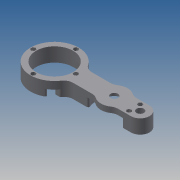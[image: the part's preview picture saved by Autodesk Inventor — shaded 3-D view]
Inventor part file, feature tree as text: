
AUTODESK INVENTOR PART (.ipt)
format: ipt  version: 2013 (Build 170138000, 138)  size: 330,752 bytes
history: native  units: mm
features: extrude x18, sketch x18, pattern_circular x2, fillet x2, projected_geometry x2, mirror x1
ambient origin geometry x8: Origin, YZ Plane, XZ Plane, XY Plane, X Axis, Y Axis, Z Axis, Center Point
bodies: Solid1 (feature_tree)
feature tree (43):
  extrude  "Extrusion1"  Depth=12.5mm
  extrude  "Extrusion2"  Depth=38.0mm TaperAngle=0.0deg
  extrude  "Extrusion3"  Depth=35.0mm
  extrude  "Extrusion4"  Depth=35.0mm TaperAngle=0.0deg
  extrude  "Extrusion5"  Depth=23.0mm TaperAngle=0.0deg
  mirror  "Mirror1"
  extrude  "Extrusion6"  Depth=4.0mm TaperAngle=0.0deg
  extrude  "Extrusion7"  Depth=4.0mm TaperAngle=0.0deg
  extrude  "Extrusion9"  Depth=7.5mm
  extrude  "Extrusion10"  Depth=7.5mm
  extrude  "Extrusion11"  Depth=3.0mm TaperAngle=0.0deg
  extrude  "Extrusion12"  Depth=1.0mm
  extrude  "Extrusion13"  Depth=1.5mm TaperAngle=0.0deg
  extrude  "Extrusion14"  Depth=7.5mm
  extrude  "Extrusion17"  Depth=1.5mm TaperAngle=0.0deg
  extrude  "Extrusion18"  Depth=5.0mm TaperAngle=0.0deg
  pattern_circular  "Circular Pattern2"  [2 undecoded]
  extrude  "Extrusion20"  Depth=3.5mm
  fillet  "Fillet1"  Radius=7.0mm
  fillet  "Fillet2"  Radius=40.0mm
  extrude  "Extrusion21"  Depth=4.0mm TaperAngle=0.0deg
  pattern_circular  "Circular Pattern3"  [2 undecoded]
  extrude  "Extrusion22"  Depth=12.5mm
  sketch  "Sketch1"  dims[d0=115.5mm d2=12.5mm]
  sketch  "Sketch2"  dims[d3=12.0mm d4=38.0mm d5=0.0mm]
  sketch  "Sketch3"  dims[d6=44.563422mm d8=35.0mm]
  sketch  "Sketch4"  dims[d9=10.0mm d10=35.0mm d11=0.0mm]
  sketch  "Sketch5"  dims[d12=50.0mm d14=23.0mm d15=0.0mm]
  sketch  "Sketch6"  dims[d16=21.0mm d19=4.0mm d20=0.0mm]
  projected_geometry  "Projected Loop1"
  sketch  "Sketch7"  dims[d22=7.5mm d23=4.0mm d24=0.0mm]
  sketch  "Sketch9"  dims[d25=3.0mm d27=7.5mm]
  sketch  "Sketch10"  dims[d28=7.5mm d29=7.5mm]
  sketch  "Sketch11"  dims[d30=7.5mm d31=3.0mm d32=0.0mm]
  sketch  "Sketch12"  dims[d36=4.0mm d37=0.0mm d43=1.0mm]
  sketch  "Sketch13"  dims[d44=1.5mm d45=0.0mm d46=1.5mm d47=0.0mm]
  sketch  "Sketch14"  dims[d50=65.0mm d51=7.5mm]
  sketch  "Sketch17"  dims[d52=1.5mm d53=0.0mm d54=1.5mm d55=0.0mm]
  sketch  "Sketch18"  dims[d56=11.4mm d57=0.0mm d58=5.0mm d59=0.0mm]
  sketch  "Sketch20"  dims[d68=44.055422mm]
  sketch  "Sketch21"  dims[d71=7.0mm d72=0.0mm]
  sketch  "Sketch22"  dims[d73=28.75mm d74=22.5mm d75=3.5mm d76=7.0mm d77=0.0mm d83=40.0mm d84=360.0deg d88=4.0mm d89=0.0mm d90=2.0mm d91=12.5mm d92=5.5mm d93=10.0mm d94=0.0mm d95=5.5mm d96=40.0mm d97=360.0deg d99=1.0mm d100=1.0mm d101=0.0mm]
  projected_geometry  "Project Cut Edges1"
note: 4 required parameter values undecoded (feature->parameter linkage not recoverable at this tier; creation-order binding heuristic only, values carry confidence <= 0.55)
